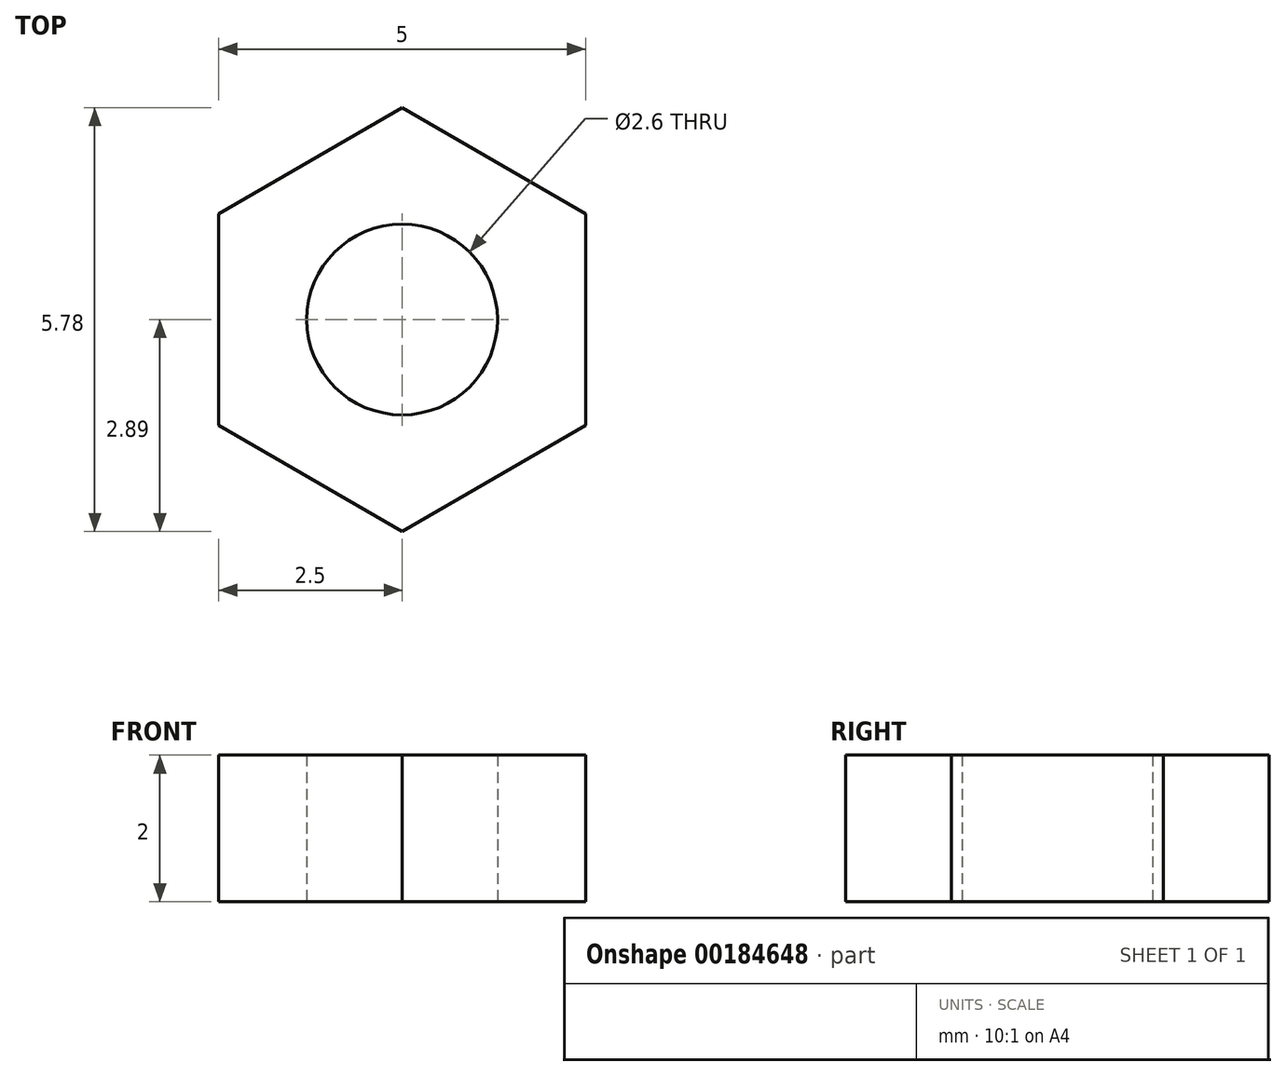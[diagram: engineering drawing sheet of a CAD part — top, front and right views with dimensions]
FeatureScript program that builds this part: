
annotation { "Feature Type Name" : "Feature", "Feature Type Description" : "" }
export const myFeature = defineFeature(function(context is Context, id is Id, definition is map)
    precondition{}
    {
        {
            var Q0;
            Q0=qCreatedBy(makeId("Top.planeOp"),FACE);
            var sketch = newSketch(context, id + "F0", { "sketchPlane" : qUnion([Q0])});
            skCircle(sketch, "E0.cCircle", {"center": v(0, 0) * mm, "radius": 2.5 * mm, "construction": true});
            skLineSegment(sketch, "E0.0", {"start": v(2.5, 1.44) * mm, "end": v(2.5, -1.44) * mm});
            skLineSegment(sketch, "E0.1", {"start": v(2.5, -1.44) * mm, "end": v(0, -2.89) * mm});
            skLineSegment(sketch, "E0.2", {"start": v(0, -2.89) * mm, "end": v(-2.5, -1.44) * mm});
            skLineSegment(sketch, "E0.3", {"start": v(-2.5, -1.44) * mm, "end": v(-2.5, 1.44) * mm});
            skLineSegment(sketch, "E0.4", {"start": v(-2.5, 1.44) * mm, "end": v(0, 2.89) * mm});
            skLineSegment(sketch, "E0.5", {"start": v(0, 2.89) * mm, "end": v(2.5, 1.44) * mm});
            skPoint(sketch, "E0.0.midPoint", {"position": v(2.5, 0) * mm});
            skCircle(sketch, "E1", {"center": v(0, 0) * mm, "radius": 1.3 * mm});
            skSolve(sketch);
        }
        {
            var Q0;
            Q0 = qSketchRegion(id + "F0", true);
            extrude(context, id + "F1", {"entities" : qUnion([Q0]), "depth" : 2 * mm, "offsetDistance" : 25 * mm});
        }
    });
